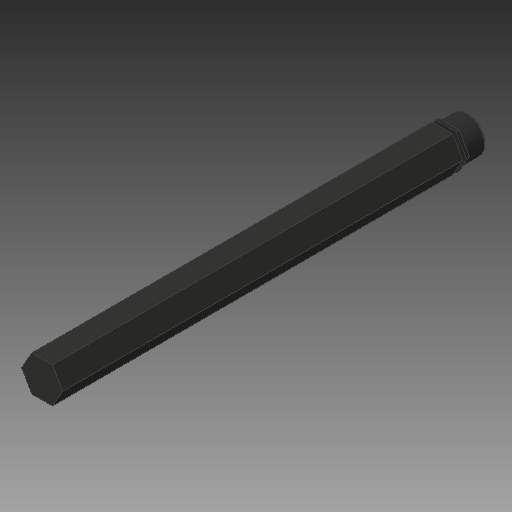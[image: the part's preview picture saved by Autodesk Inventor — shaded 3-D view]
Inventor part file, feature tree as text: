
AUTODESK INVENTOR PART (.ipt)
format: ipt  version: 2017 (Build 210142000, 142)  size: 100,864 bytes
history: native  units: in
note: dims shown in document units (in); Inventor stores cm internally (conversion verified against a paired STEP export)
features: chamfer x1
ambient origin geometry x8: Origin, YZ Plane, XZ Plane, XY Plane, X Axis, Y Axis, Z Axis, Center Point
bodies: Solid1 (feature_tree)
feature tree (1):
  chamfer  "Chamfer1"  [1 undecoded]
note: 1 required parameter value undecoded (feature->parameter linkage not recoverable at this tier; creation-order binding heuristic only, values carry confidence <= 0.55)
